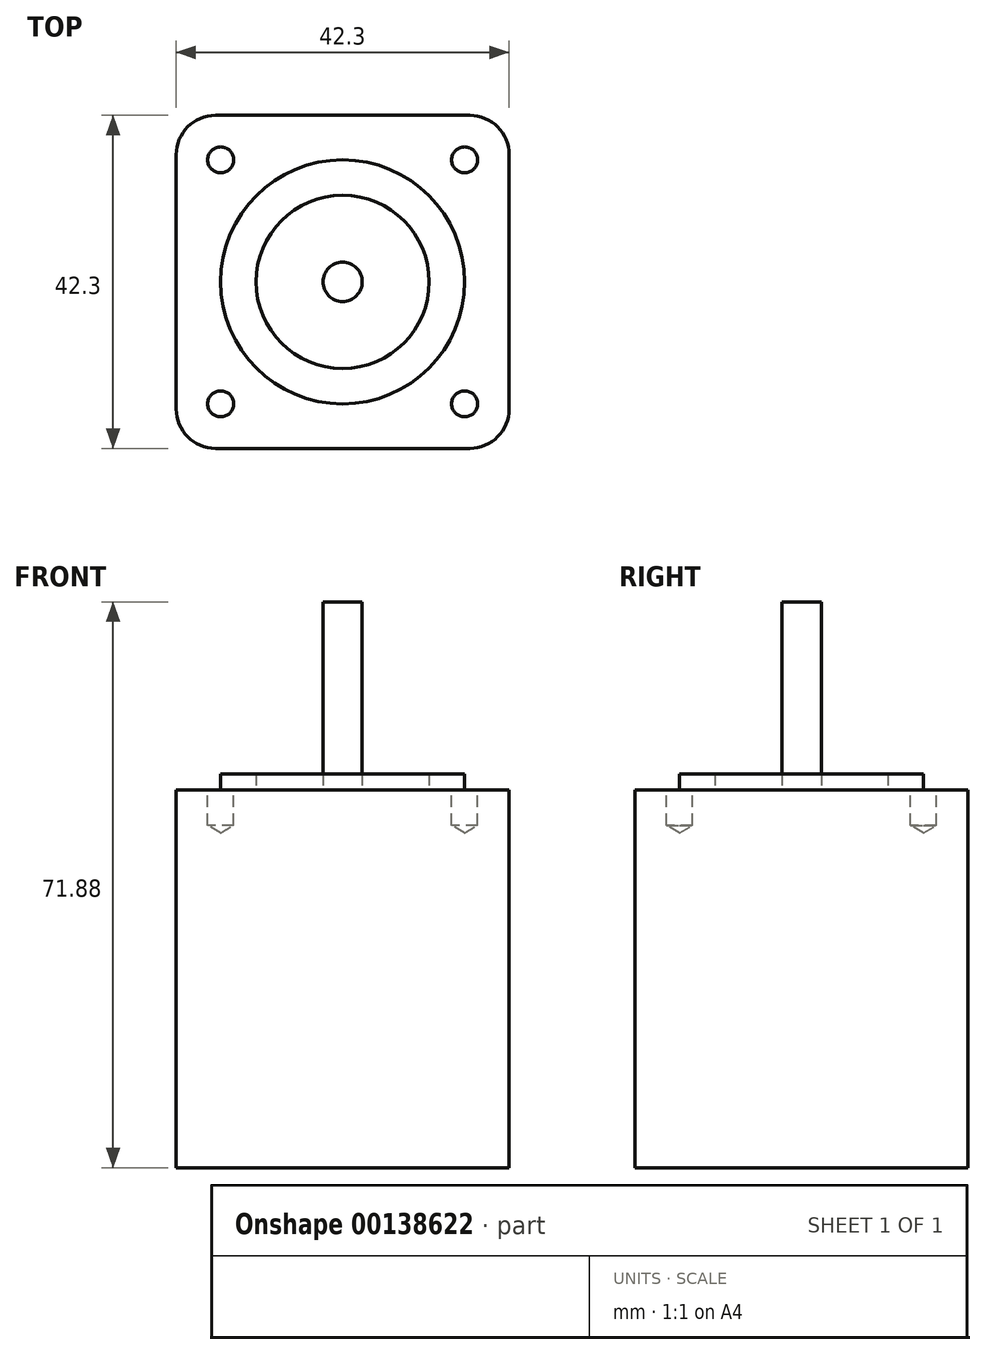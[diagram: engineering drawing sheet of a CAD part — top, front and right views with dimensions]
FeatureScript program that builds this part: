
annotation { "Feature Type Name" : "Feature", "Feature Type Description" : "" }
export const myFeature = defineFeature(function(context is Context, id is Id, definition is map)
    precondition{}
    {
        {
            var Q0;
            Q0=qCreatedBy(makeId("Top.planeOp"),FACE);
            var sketch = newSketch(context, id + "F0", { "sketchPlane" : qUnion([Q0])});
            skLineSegment(sketch, "E0.bottom", {"start": v(21.15, -21.15) * mm, "end": v(-21.15, -21.15) * mm});
            skLineSegment(sketch, "E0.top", {"start": v(21.15, 21.15) * mm, "end": v(-21.15, 21.15) * mm});
            skLineSegment(sketch, "E0.left", {"start": v(21.15, -21.15) * mm, "end": v(21.15, 21.15) * mm});
            skLineSegment(sketch, "E0.right", {"start": v(-21.15, -21.15) * mm, "end": v(-21.15, 21.15) * mm});
            skPoint(sketch, "E0.middle", {"position": v(0, 0) * mm});
            skLineSegment(sketch, "E1.bottom", {"start": v(15.5, -15.5) * mm, "end": v(-15.5, -15.5) * mm, "construction": true});
            skLineSegment(sketch, "E1.top", {"start": v(15.5, 15.5) * mm, "end": v(-15.5, 15.5) * mm, "construction": true});
            skLineSegment(sketch, "E1.left", {"start": v(15.5, -15.5) * mm, "end": v(15.5, 15.5) * mm, "construction": true});
            skLineSegment(sketch, "E1.right", {"start": v(-15.5, -15.5) * mm, "end": v(-15.5, 15.5) * mm, "construction": true});
            skSolve(sketch);
        }
        {
            var Q0;
            Q0 = qSketchRegion(id + "F0", true);
            extrude(context, id + "F1", {"entities" : qUnion([Q0]), "oppositeDirection" : true, "depth" : 48 * mm});
        }
        {
            var Q0;
            Q0=sQuery(id+"F0.wireOp",VERTEX,"E1.right.end");
            var Q1;
            Q1=sQuery(id+"F0.wireOp",VERTEX,"E1.right.start");
            var Q2;
            Q2=sQuery(id+"F0.wireOp",VERTEX,"E1.left.start");
            var Q3;
            Q3=sQuery(id+"F0.wireOp",VERTEX,"E1.left.end");
            var Q4;
            Q4=makeQuery(id+"F1.opExtrude","SWEPT_BODY",BODY,{"disambiguationData":[OSD([sQuery(id+"F0.wireOp",EDGE,"E0.bottom"),sQuery(id+"F0.wireOp",EDGE,"E0.top"),sQuery(id+"F0.wireOp",EDGE,"E0.left"),sQuery(id+"F0.wireOp",EDGE,"E0.right")])]});
            hole(context, id + "F2", {"style" : HoleStyle.SIMPLE, "endStyle" : HoleEndStyle.BLIND, "standardTappedOrClearance" : lookupTablePath({ "standard" : "ISO", "fit" : "Normal", "size" : "M3", "type" : "Clearance" }), "standardBlindInLast" : lookupTablePath({ "fit" : "Standard", "standard" : "ISO", "size" : "M3", "type" : "Clearance" }), "holeDiameter" : 3.3 * mm, "holeDepth" : 4.5 * mm, "startFromSketch" : true, "locations" : qUnion([Q0, Q1, Q2, Q3]), "scope" : qUnion([Q4])});
        }
        {
            var Q0;
            Q0=makeQuery(id+"F1.opExtrude","SWEPT_EDGE",EDGE,{"disambiguationData":[OSD([sQuery(id+"F0.wireOp",EDGE,"E0.top"),sQuery(id+"F0.wireOp",EDGE,"E0.right")])]});
            var Q1;
            Q1=makeQuery(id+"F1.opExtrude","SWEPT_EDGE",EDGE,{"disambiguationData":[OSD([sQuery(id+"F0.wireOp",EDGE,"E0.bottom"),sQuery(id+"F0.wireOp",EDGE,"E0.right")])]});
            var Q2;
            Q2=makeQuery(id+"F1.opExtrude","SWEPT_EDGE",EDGE,{"disambiguationData":[OSD([sQuery(id+"F0.wireOp",EDGE,"E0.bottom"),sQuery(id+"F0.wireOp",EDGE,"E0.left")])]});
            var Q3;
            Q3=makeQuery(id+"F1.opExtrude","SWEPT_EDGE",EDGE,{"disambiguationData":[OSD([sQuery(id+"F0.wireOp",EDGE,"E0.top"),sQuery(id+"F0.wireOp",EDGE,"E0.left")])]});
            fillet(context, id + "F3", {"entities" : qUnion([Q0, Q1, Q2, Q3]), "radius" : 5 * mm, "tangentPropagation" : true, "allowEdgeOverflow" : false});
        }
        {
            var Q0;
            Q0=makeQuery(id+"F0.imprint","IMPRINT",FACE,{"disambiguationData":[TD([[makeQuery(id+"F0.imprint","IMPRINT",EDGE,{"derivedFrom":sQuery(id+"F0.wireOp",EDGE,"E0.bottom")}),-1.0]])]});
            var sketch = newSketch(context, id + "F4", { "sketchPlane" : qUnion([Q0])});
            skCircle(sketch, "E2", {"center": v(0, 0) * mm, "radius": 11 * mm});
            skCircle(sketch, "E3", {"center": v(0, 0) * mm, "radius": 15.5 * mm});
            skSolve(sketch);
        }
        {
            var Q0;
            Q0 = qSketchRegion(id + "F4", true);
            extrude(context, id + "F5", {"entities" : qUnion([Q0]), "operationType" : NewBodyOperationType.ADD, "depth" : 2.03 * mm});
        }
        {
            var Q0;
            Q0=makeQuery(id+"F0.imprint","IMPRINT",FACE,{"disambiguationData":[TD([[makeQuery(id+"F0.imprint","IMPRINT",EDGE,{"derivedFrom":sQuery(id+"F0.wireOp",EDGE,"E0.bottom")}),-1.0]])]});
            var sketch = newSketch(context, id + "F6", { "sketchPlane" : qUnion([Q0])});
            skCircle(sketch, "E4", {"center": v(0, 0) * mm, "radius": 2.5 * mm});
            skSolve(sketch);
        }
        {
            var Q0;
            Q0 = qSketchRegion(id + "F6", true);
            extrude(context, id + "F7", {"entities" : qUnion([Q0]), "operationType" : NewBodyOperationType.ADD, "depth" : 23.88 * mm});
        }
    });
